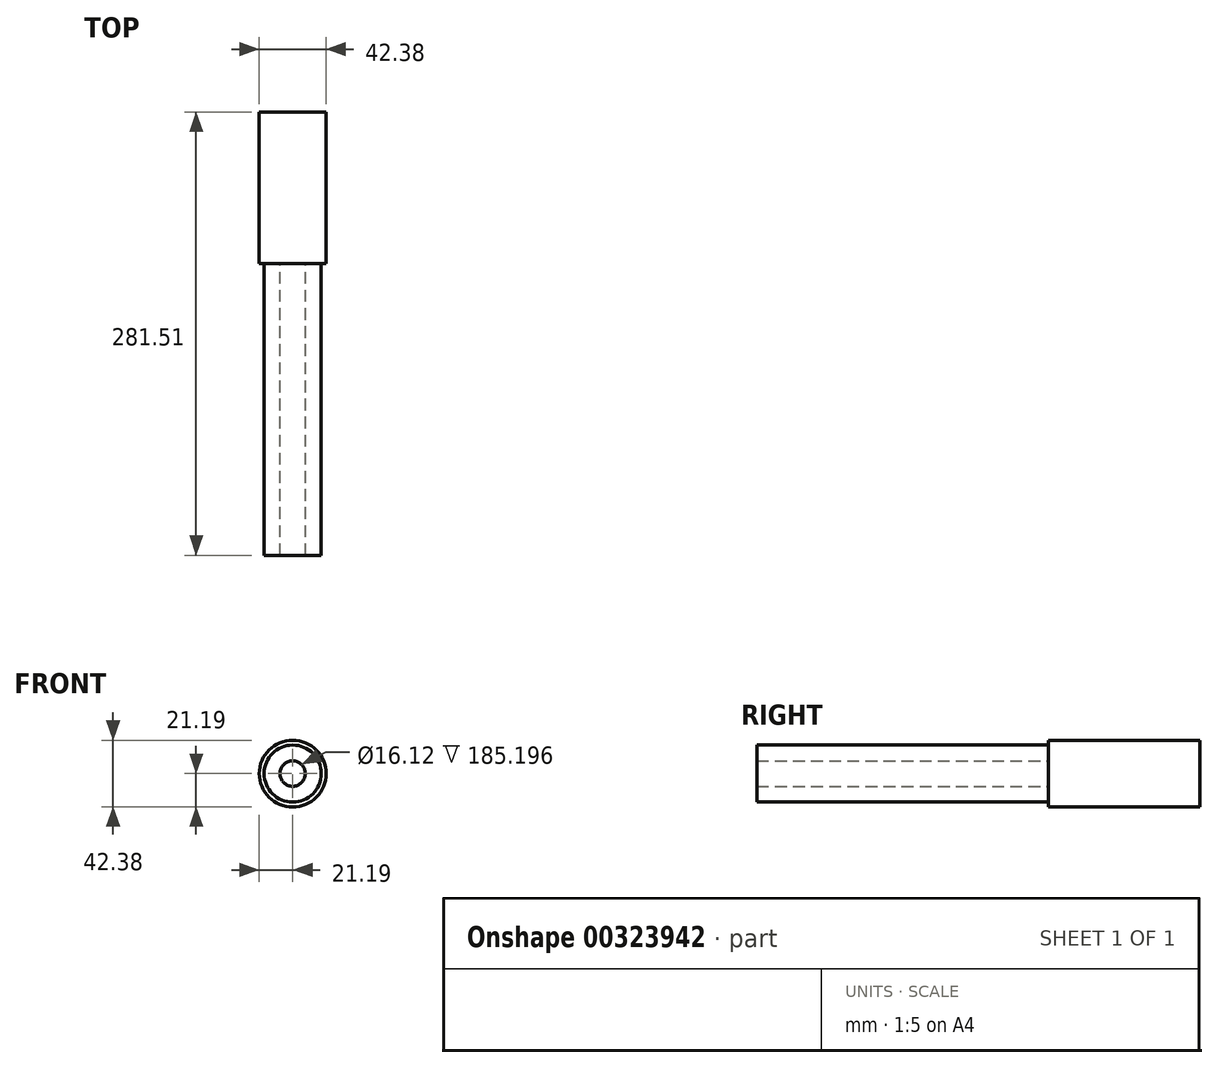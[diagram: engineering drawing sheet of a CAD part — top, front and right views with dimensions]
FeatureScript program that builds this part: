
annotation { "Feature Type Name" : "Feature", "Feature Type Description" : "" }
export const myFeature = defineFeature(function(context is Context, id is Id, definition is map)
    precondition{}
    {
        {
            var Q0;
            Q0=qCreatedBy(makeId("Front.planeOp"),FACE);
            var sketch = newSketch(context, id + "F0", { "sketchPlane" : qUnion([Q0])});
            skCircle(sketch, "E0", {"center": v(0, 0) * mm, "radius": 18.13 * mm});
            skCircle(sketch, "E1", {"center": v(0, 0) * mm, "radius": 8.06 * mm});
            skSolve(sketch);
        }
        {
            var Q0;
            Q0=makeQuery(id+"F0.imprint","IMPRINT",FACE,{"disambiguationData":[TD([[makeQuery(id+"F0.imprint","IMPRINT",EDGE,{"derivedFrom":sQuery(id+"F0.wireOp",EDGE,"E0")}),1.0]])]});
            extrude(context, id + "F1", {"entities" : qUnion([Q0]), "depth" : 185.2 * mm});
        }
        {
            var Q0;
            Q0=qCreatedBy(makeId("Front.planeOp"),FACE);
            var sketch = newSketch(context, id + "F2", { "sketchPlane" : qUnion([Q0])});
            skCircle(sketch, "E2", {"center": v(0, 0) * mm, "radius": 21.2 * mm});
            skSolve(sketch);
        }
        {
            var Q0;
            Q0=makeQuery(id+"F2.imprint","IMPRINT",FACE,{"disambiguationData":[TD([[makeQuery(id+"F2.imprint","IMPRINT",EDGE,{"derivedFrom":sQuery(id+"F2.wireOp",EDGE,"E2")}),1.0]])]});
            extrude(context, id + "F3", {"entities" : qUnion([Q0]), "operationType" : NewBodyOperationType.ADD, "oppositeDirection" : true, "depth" : 96.3 * mm});
        }
    });
